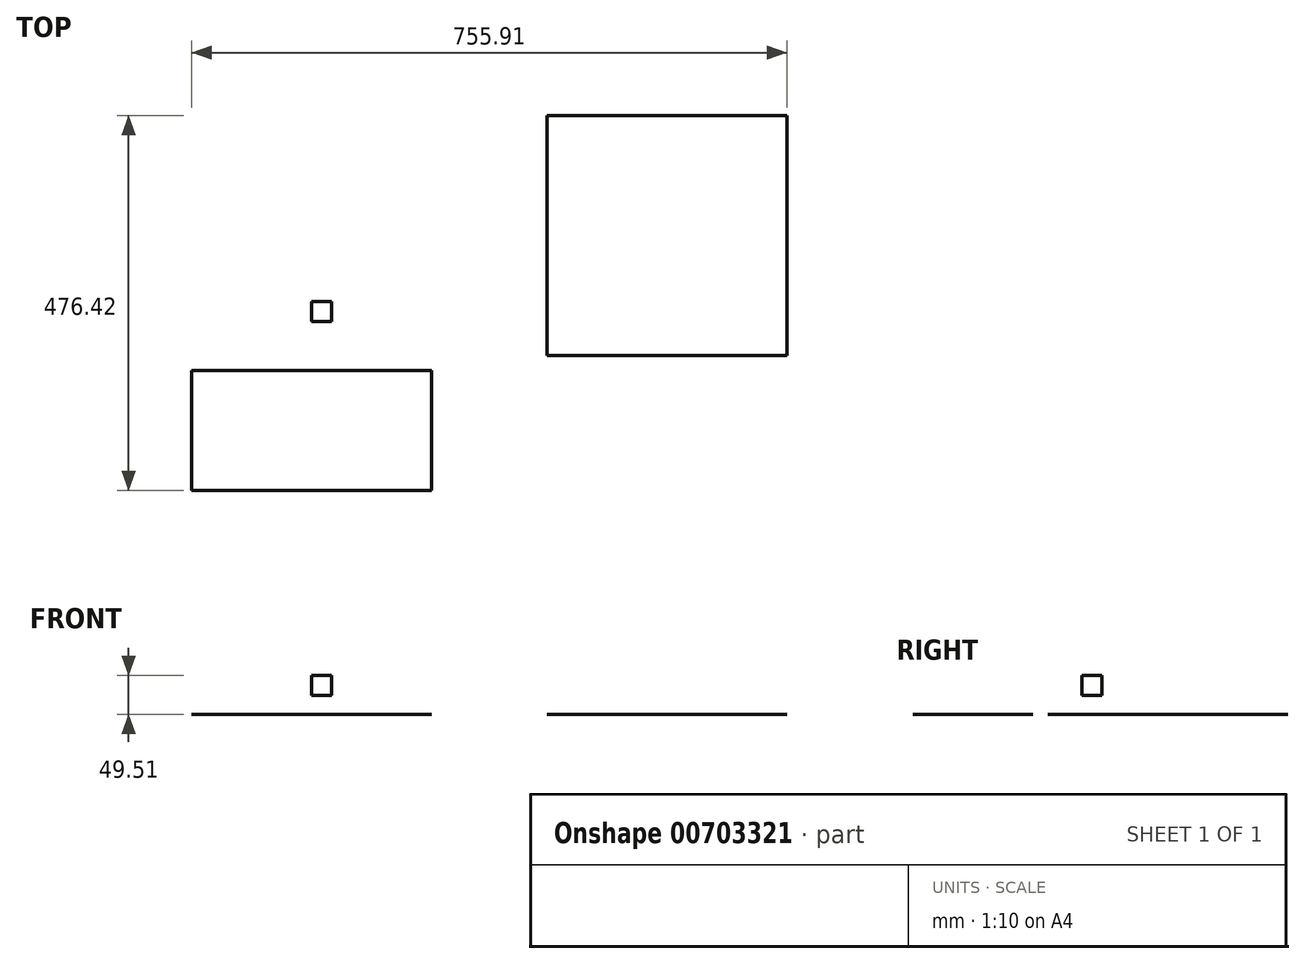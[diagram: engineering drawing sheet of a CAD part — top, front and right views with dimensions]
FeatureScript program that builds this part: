
annotation { "Feature Type Name" : "Feature", "Feature Type Description" : "" }
export const myFeature = defineFeature(function(context is Context, id is Id, definition is map)
    precondition{}
    {
        {
            var Q0;
            Q0=qCreatedBy(makeId("Top.planeOp"),FACE);
            var sketch = newSketch(context, id + "F0", { "sketchPlane" : qUnion([Q0])});
            skLineSegment(sketch, "E0.bottom", {"start": v(152.4, 76.2) * mm, "end": v(-152.4, 76.2) * mm});
            skLineSegment(sketch, "E0.top", {"start": v(152.4, -76.2) * mm, "end": v(-152.4, -76.2) * mm});
            skLineSegment(sketch, "E0.left", {"start": v(152.4, 76.2) * mm, "end": v(152.4, -76.2) * mm});
            skLineSegment(sketch, "E0.right", {"start": v(-152.4, 76.2) * mm, "end": v(-152.4, -76.2) * mm});
            skPoint(sketch, "E0.middle", {"position": v(0, 0) * mm});
            skSolve(sketch);
        }
        {
            var Q0;
            Q0 = qSketchRegion(id + "F0", true);
            extrude(context, id + "F1", {"entities" : qUnion([Q0]), "depth" : 1 / 406.4 * mm, "offsetDistance" : 25 * mm});
        }
        {
            var Q0;
            Q0=qCreatedBy(makeId("Top.planeOp"),FACE);
            var sketch = newSketch(context, id + "F2", { "sketchPlane" : qUnion([Q0])});
            skLineSegment(sketch, "E1.bottom", {"start": v(603.51, 95.42) * mm, "end": v(298.71, 95.42) * mm});
            skLineSegment(sketch, "E1.top", {"start": v(603.51, 400.22) * mm, "end": v(298.71, 400.22) * mm});
            skLineSegment(sketch, "E1.left", {"start": v(603.51, 95.42) * mm, "end": v(603.51, 400.22) * mm});
            skLineSegment(sketch, "E1.right", {"start": v(298.71, 95.42) * mm, "end": v(298.71, 400.22) * mm});
            skPoint(sketch, "E1.middle", {"position": v(451.11, 247.82) * mm});
            skSolve(sketch);
        }
        {
            var Q0;
            Q0=makeQuery(id+"F2.imprint","IMPRINT",FACE,{"disambiguationData":[TD([[makeQuery(id+"F2.imprint","IMPRINT",EDGE,{"derivedFrom":sQuery(id+"F2.wireOp",EDGE,"E1.bottom")}),-1.0]])]});
            extrude(context, id + "F3", {"entities" : qUnion([Q0]), "depth" : 1 / 406.4 * mm, "offsetDistance" : 25 * mm});
        }
        {
            var Q0;
            Q0=qCreatedBy(makeId("Right.planeOp"),FACE);
            var sketch = newSketch(context, id + "F4", { "sketchPlane" : qUnion([Q0])});
            skLineSegment(sketch, "E2.bottom", {"start": v(138.65, 24.11) * mm, "end": v(164.05, 24.11) * mm});
            skLineSegment(sketch, "E2.top", {"start": v(138.65, 49.51) * mm, "end": v(164.05, 49.51) * mm});
            skLineSegment(sketch, "E2.left", {"start": v(138.65, 24.11) * mm, "end": v(138.65, 49.51) * mm});
            skLineSegment(sketch, "E2.right", {"start": v(164.05, 24.11) * mm, "end": v(164.05, 49.51) * mm});
            skSolve(sketch);
        }
        {
            var Q0;
            Q0=makeQuery(id+"F4.imprint","IMPRINT",FACE,{"disambiguationData":[TD([[makeQuery(id+"F4.imprint","IMPRINT",EDGE,{"derivedFrom":sQuery(id+"F4.wireOp",EDGE,"E2.bottom")}),1.0]])]});
            extrude(context, id + "F5", {"entities" : qUnion([Q0]), "depth" : 25.4 * mm, "offsetDistance" : 25 * mm});
        }
    });
